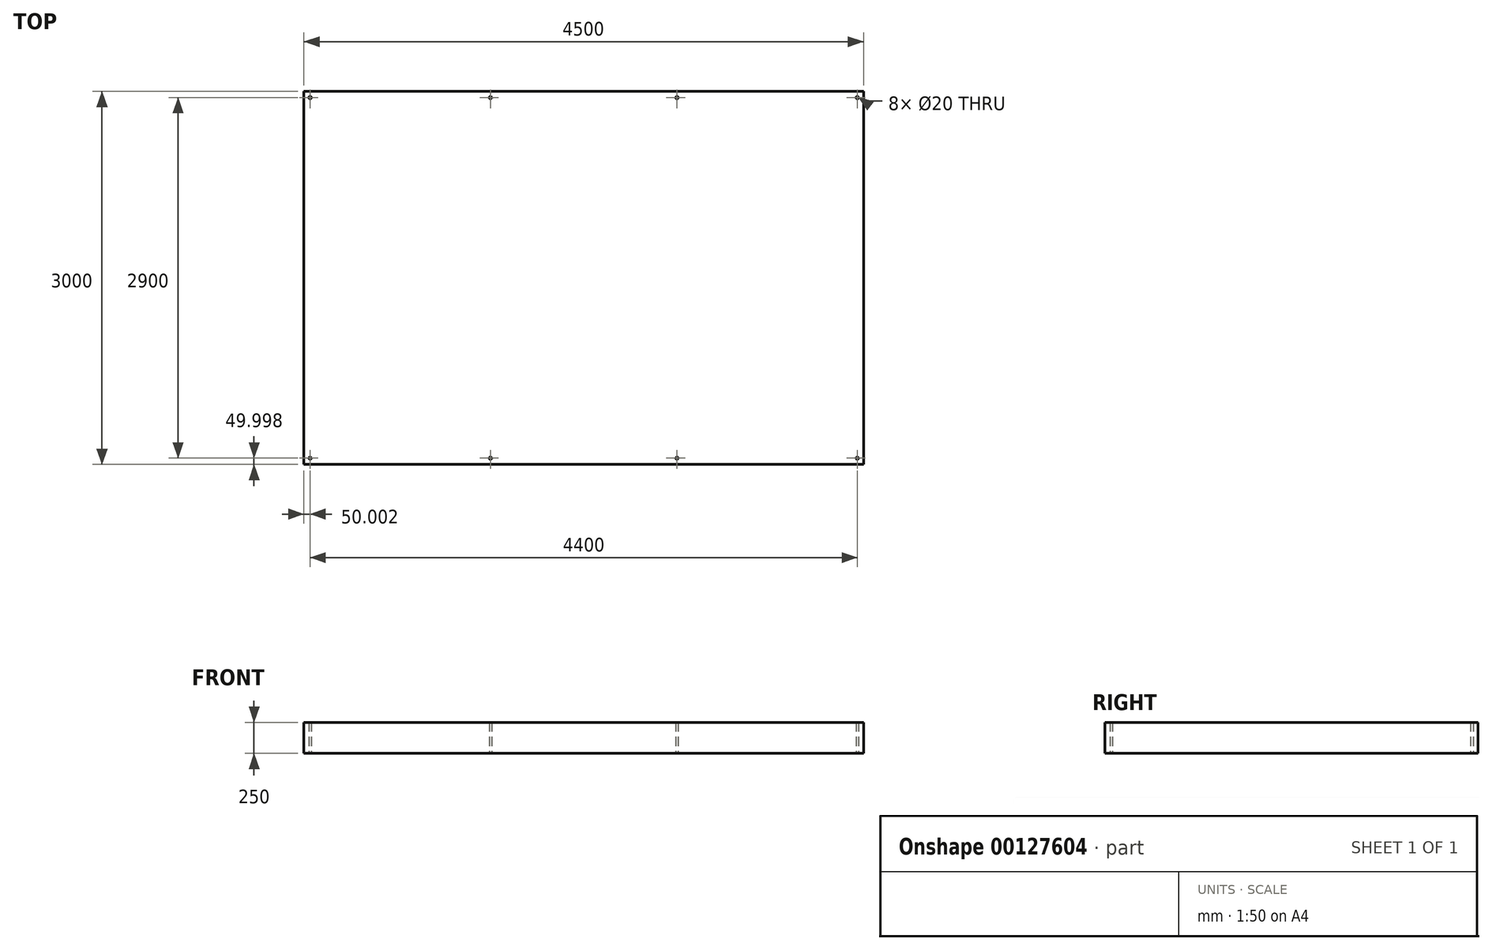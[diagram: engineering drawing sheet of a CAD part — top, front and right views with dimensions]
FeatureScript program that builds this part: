
annotation { "Feature Type Name" : "Feature", "Feature Type Description" : "" }
export const myFeature = defineFeature(function(context is Context, id is Id, definition is map)
    precondition{}
    {
        {
            var Q0;
            Q0=qCreatedBy(makeId("Top.planeOp"),FACE);
            var sketch = newSketch(context, id + "F0", { "sketchPlane" : qUnion([Q0])});
            skLineSegment(sketch, "E0.bottom", {"start": v(-2250.3, 1976.66) * mm, "end": v(2249.7, 1976.66) * mm});
            skLineSegment(sketch, "E0.top", {"start": v(-2250.3, -1023.34) * mm, "end": v(2249.7, -1023.34) * mm});
            skLineSegment(sketch, "E0.left", {"start": v(-2250.3, 1976.66) * mm, "end": v(-2250.3, -1023.34) * mm});
            skLineSegment(sketch, "E0.right", {"start": v(2249.7, 1976.66) * mm, "end": v(2249.7, -1023.34) * mm});
            skLineSegment(sketch, "E1", {"start": v(-2250.3, -973.34) * mm, "end": v(2249.7, -973.34) * mm, "construction": true});
            skCircle(sketch, "E2", {"center": v(-2200.3, -973.34) * mm, "radius": 10 * mm});
            skCircle(sketch, "E3", {"center": v(-750.3, -973.34) * mm, "radius": 10 * mm});
            skCircle(sketch, "E4", {"center": v(749.7, -973.34) * mm, "radius": 10 * mm});
            skCircle(sketch, "E5", {"center": v(2199.7, -973.34) * mm, "radius": 10 * mm});
            skLineSegment(sketch, "E6", {"start": v(-1023.4, 476.66) * mm, "end": v(-552.76, 476.66) * mm, "construction": true});
            skPoint(sketch, "E6.startSnap0", {"position": v(-2250.3, 476.66) * mm});
            skCircle(sketch, "E7.MirrorC", {"center": v(-2200.3, 1926.66) * mm, "radius": 10 * mm});
            skCircle(sketch, "E8.MirrorC", {"center": v(-750.3, 1926.66) * mm, "radius": 10 * mm});
            skCircle(sketch, "E9.MirrorC", {"center": v(749.7, 1926.66) * mm, "radius": 10 * mm});
            skCircle(sketch, "E10.MirrorC", {"center": v(2199.7, 1926.66) * mm, "radius": 10 * mm});
            skSolve(sketch);
        }
        {
            var Q0;
            Q0=makeQuery(id+"F0.imprint","IMPRINT",FACE,{"disambiguationData":[TD([[makeQuery(id+"F0.imprint","IMPRINT",EDGE,{"derivedFrom":sQuery(id+"F0.wireOp",EDGE,"E0.bottom")}),-1.0]])]});
            extrude(context, id + "F1", {"entities" : qUnion([Q0]), "depth" : 250 * mm});
        }
    });
